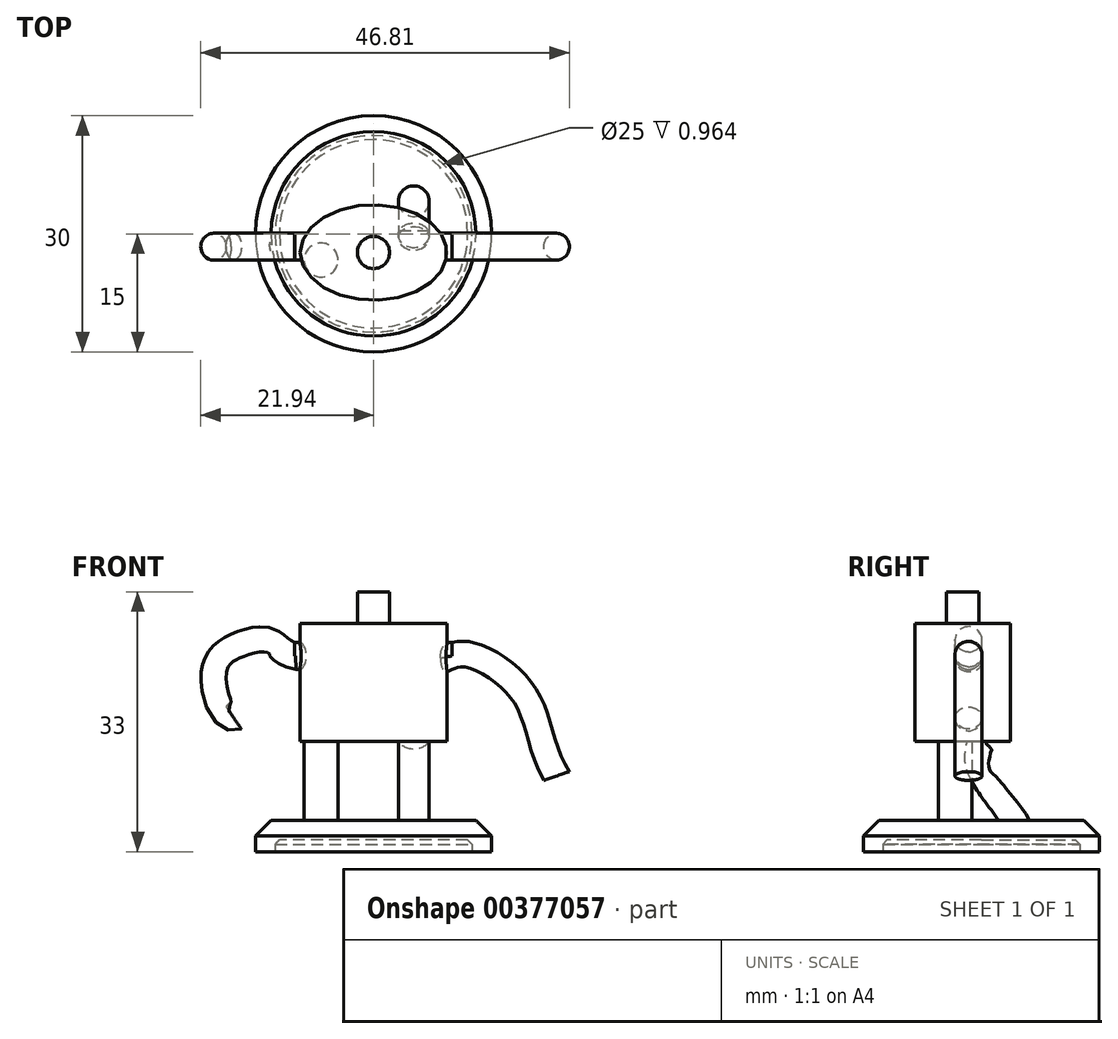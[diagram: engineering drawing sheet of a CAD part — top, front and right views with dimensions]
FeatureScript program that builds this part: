
annotation { "Feature Type Name" : "Feature", "Feature Type Description" : "" }
export const myFeature = defineFeature(function(context is Context, id is Id, definition is map)
    precondition{}
    {
        {
            var Q0;
            Q0=qCreatedBy(makeId("Top.planeOp"),FACE);
            var sketch = newSketch(context, id + "F0", { "sketchPlane" : qUnion([Q0])});
            skCircle(sketch, "E0", {"center": v(0, 0) * mm, "radius": 15 * mm});
            skSolve(sketch);
        }
        {
            var Q0;
            Q0=makeQuery(id+"F0.imprint","IMPRINT",FACE,{"disambiguationData":[TD([[makeQuery(id+"F0.imprint","IMPRINT",EDGE,{"derivedFrom":sQuery(id+"F0.wireOp",EDGE,"E0")}),1.0]])]});
            extrude(context, id + "F1", {"entities" : qUnion([Q0]), "depth" : 4 * mm});
        }
        {
            var Q0;
            Q0=makeQuery(id+"F1.opExtrude","CAP_EDGE",EDGE,{"disambiguationData":[OSD([sQuery(id+"F0.wireOp",EDGE,"E0")])],"isStart":false});
            chamfer(context, id + "F2", {"entities" : qUnion([Q0]), "width" : 2 * mm, "tangentPropagation" : true});
        }
        {
            var Q0;
            Q0=makeQuery(id+"F1.opExtrude","CAP_FACE",FACE,{"disambiguationData":[OSD([sQuery(id+"F0.wireOp",EDGE,"E0")])],"isStart":true});
            shell(context, id + "F3", {"entities" : qUnion([Q0]), "thickness" : 2.5 * mm});
        }
        {
            var Q0;
            Q0=makeQuery(id+"F1.opExtrude","CAP_FACE",FACE,{"disambiguationData":[OSD([sQuery(id+"F0.wireOp",EDGE,"E0")])],"isStart":false});
            cPlane(context, id + "F4", {"entities" : qUnion([Q0]), "cplaneType" : CPlaneType.OFFSET, "offset" : 0 * mm, "width" : 150 * mm, "height" : 150 * mm});
        }
        {
            var Q0;
            Q0=qCreatedBy(id+"F4.planeOp",FACE);
            var sketch = newSketch(context, id + "F5", { "sketchPlane" : qUnion([Q0])});
            skCircle(sketch, "E1", {"center": v(-6.67, -3.33) * mm, "radius": 2.16 * mm});
            skCircle(sketch, "E2", {"center": v(5.1, 4.15) * mm, "radius": 1.95 * mm});
            skSolve(sketch);
        }
        {
            var Q0;
            Q0=makeQuery(id+"F5.imprint","IMPRINT",FACE,{"disambiguationData":[TD([[makeQuery(id+"F5.imprint","IMPRINT",EDGE,{"derivedFrom":sQuery(id+"F5.wireOp",EDGE,"E1")}),1.0]])]});
            extrude(context, id + "F6", {"entities" : qUnion([Q0]), "operationType" : NewBodyOperationType.ADD, "depth" : 10 * mm});
        }
        {
            var Q0;
            Q0=qCreatedBy(makeId("Right.planeOp"),FACE);
            cPlane(context, id + "F7", {"entities" : qUnion([Q0]), "cplaneType" : CPlaneType.OFFSET, "offset" : 3 * mm, "width" : 150 * mm, "height" : 150 * mm});
        }
        {
            var Q0;
            Q0=qCreatedBy(id+"F7.planeOp",FACE);
            var sketch = newSketch(context, id + "F8", { "sketchPlane" : qUnion([Q0])});
            skFitSpline(sketch, "E3", {"points": [v(3.01, 3.6) * mm, v(0, 7.8) * mm, v(-1.59, 11.57) * mm, v(-0.94, 15.49) * mm], "startDerivative": vector(-5.72, 9.6) * mm, "endDerivative": vector(3.85, 15.23) * mm});
            skSolve(sketch);
        }
        {
            var Q0;
            Q0=makeQuery(id+"F5.imprint","IMPRINT",FACE,{"disambiguationData":[TD([[makeQuery(id+"F5.imprint","IMPRINT",EDGE,{"derivedFrom":sQuery(id+"F5.wireOp",EDGE,"E2")}),1.0]])]});
            var Q1;
            Q1=sQuery(id+"F8.wireOp",EDGE,"E3");
            sweep(context, id + "F9", {"operationType" : NewBodyOperationType.ADD, "profiles" : qUnion([Q0]), "path" : qUnion([Q1])});
        }
        {
            var Q0;
            Q0=makeQuery(id+"F6.opExtrude","CAP_FACE",FACE,{"disambiguationData":[OSD([sQuery(id+"F5.wireOp",EDGE,"E1")])],"isStart":false});
            var sketch = newSketch(context, id + "F10", { "sketchPlane" : qUnion([Q0])});
            skEllipse(sketch, "E4", {"center": v(0, -2.37) * mm, "majorRadius": 9.31 * mm, "minorRadius": 6.06 * mm, "majorAxis": v(-1, 0)});
            skSolve(sketch);
        }
        {
            var Q0;
            Q0=makeQuery(id+"F10.imprint","IMPRINT",FACE,{"disambiguationData":[TD([[makeQuery(id+"F10.imprint","IMPRINT",EDGE,{"derivedFrom":sQuery(id+"F10.wireOp",EDGE,"E4")}),1.0]])]});
            var Q1;
            Q1=makeQuery(id+"F10.imprint","IMPRINT",FACE,{"disambiguationData":[TD([[makeQuery(id+"F10.imprint","IMPRINT",EDGE,{"derivedFrom":makeQuery(id+"F6.opExtrude","CAP_EDGE",EDGE,{"disambiguationData":[OSD([sQuery(id+"F5.wireOp",EDGE,"E1")])],"isStart":false})}),1.0]])]});
            extrude(context, id + "F11", {"entities" : qUnion([Q0, Q1]), "operationType" : NewBodyOperationType.ADD, "depth" : 15 * mm});
        }
        {
            var Q0;
            Q0=makeQuery(id+"F11.opExtrude","CAP_FACE",FACE,{"disambiguationData":[OSD([sQuery(id+"F10.wireOp",EDGE,"E4")])],"isStart":false});
            var sketch = newSketch(context, id + "F12", { "sketchPlane" : qUnion([Q0])});
            skCircle(sketch, "E5", {"center": v(0, -2.37) * mm, "radius": 2.04 * mm});
            skSolve(sketch);
        }
        {
            var Q0;
            Q0=makeQuery(id+"F12.imprint","IMPRINT",FACE,{"disambiguationData":[TD([[makeQuery(id+"F12.imprint","IMPRINT",EDGE,{"derivedFrom":sQuery(id+"F12.wireOp",EDGE,"E5")}),1.0]])]});
            extrude(context, id + "F13", {"entities" : qUnion([Q0]), "operationType" : NewBodyOperationType.ADD, "depth" : 4 * mm});
        }
        {
            var Q0;
            Q0=qCreatedBy(makeId("Right.planeOp"),FACE);
            var sketch = newSketch(context, id + "F14", { "sketchPlane" : qUnion([Q0])});
            skCircle(sketch, "E6", {"center": v(-1.63, 24.88) * mm, "radius": 1.7 * mm});
            skSolve(sketch);
        }
        {
            var Q0;
            Q0 = qSketchRegion(id + "F14", true);
            extrude(context, id + "F15", {"entities" : qUnion([Q0]), "operationType" : NewBodyOperationType.ADD, "depth" : 10 * mm});
        }
        {
            var Q0;
            Q0 = qSketchRegion(id + "F14", true);
            extrude(context, id + "F16", {"entities" : qUnion([Q0]), "operationType" : NewBodyOperationType.ADD, "oppositeDirection" : true, "depth" : 10 * mm});
        }
        {
            var Q0;
            Q0=qCreatedBy(makeId("Front.planeOp"),FACE);
            var sketch = newSketch(context, id + "F17", { "sketchPlane" : qUnion([Q0])});
            skFitSpline(sketch, "E7", {"points": [v(-17.25, 16.26) * mm, v(-21.12, 22.73) * mm, v(-17.33, 27.09) * mm, v(-12.93, 27.56) * mm, v(-9.92, 25.73) * mm], "startDerivative": vector(-24.5, -7.93) * mm, "endDerivative": vector(18.77, -5.09) * mm});
            skFitSpline(sketch, "E8", {"points": [v(7.94, 25.37) * mm, v(12.16, 26.21) * mm, v(20.32, 20.35) * mm, v(24.42, 10.02) * mm], "startDerivative": vector(15.76, 6.21) * mm, "endDerivative": vector(16.36, -25.45) * mm});
            skSolve(sketch);
        }
        {
            var Q0;
            Q0=makeQuery(id+"F16.opExtrude","CAP_FACE",FACE,{"disambiguationData":[OSD([sQuery(id+"F14.wireOp",EDGE,"E6")])],"isStart":false});
            var Q1;
            Q1=sQuery(id+"F17.wireOp",EDGE,"E7");
            sweep(context, id + "F18", {"operationType" : NewBodyOperationType.ADD, "profiles" : qUnion([Q0]), "path" : qUnion([Q1])});
        }
        {
            var Q0;
            Q0=makeQuery(id+"F15.opExtrude","CAP_FACE",FACE,{"disambiguationData":[OSD([sQuery(id+"F14.wireOp",EDGE,"E6")])],"isStart":false});
            var Q1;
            Q1=sQuery(id+"F17.wireOp",EDGE,"E8");
            sweep(context, id + "F19", {"operationType" : NewBodyOperationType.ADD, "profiles" : qUnion([Q0]), "path" : qUnion([Q1])});
        }
    });
